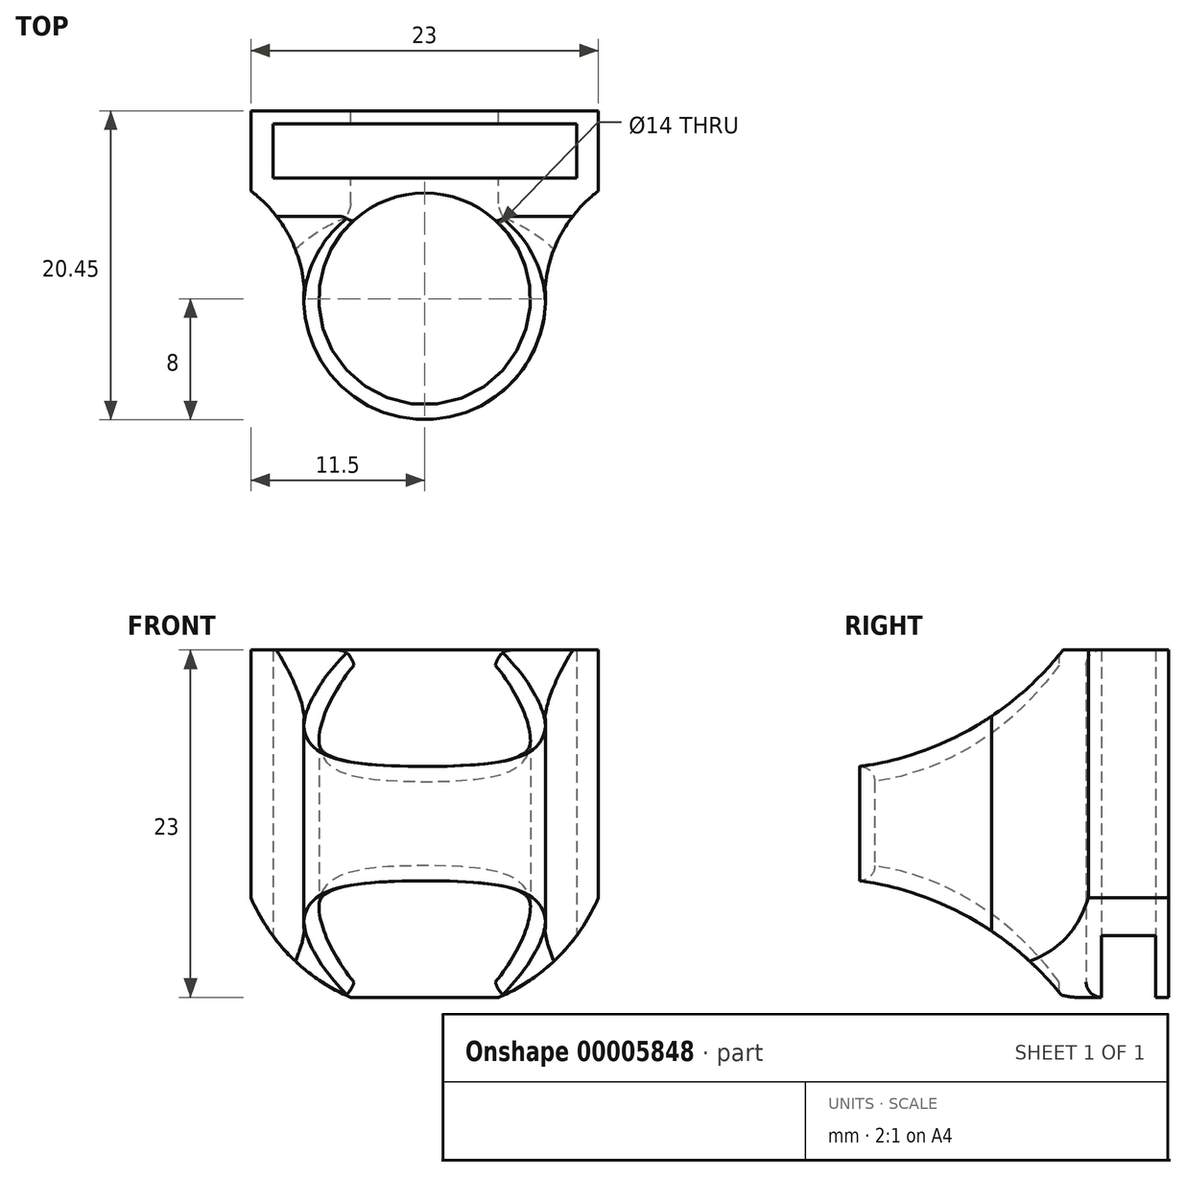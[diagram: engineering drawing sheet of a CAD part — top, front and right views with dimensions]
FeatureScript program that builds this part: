
annotation { "Feature Type Name" : "Feature", "Feature Type Description" : "" }
export const myFeature = defineFeature(function(context is Context, id is Id, definition is map)
    precondition{}
    {
        {
            var Q0;
            Q0=qCreatedBy(makeId("Top.planeOp"),FACE);
            var sketch = newSketch(context, id + "F0", { "sketchPlane" : qUnion([Q0])});
            skCircle(sketch, "E0", {"center": v(0, 0) * mm, "radius": 7 * mm});
            skArc(sketch, "E1", {"start": v(-7.97, 0.72) * mm, "mid": v(0, -8) * mm, "end": v(7.97, 0.72) * mm});
            skLineSegment(sketch, "E2.rect.bottom", {"start": v(11.5, 7.15) * mm, "end": v(-11.5, 7.15) * mm, "construction": true});
            skLineSegment(sketch, "E2.rect.top", {"start": v(11.5, 12.45) * mm, "end": v(-11.5, 12.45) * mm});
            skLineSegment(sketch, "E2.rect.left", {"start": v(11.5, 7.15) * mm, "end": v(11.5, 12.45) * mm});
            skLineSegment(sketch, "E2.rect.right", {"start": v(-11.5, 7.15) * mm, "end": v(-11.5, 12.45) * mm});
            skPoint(sketch, "E2.rect.middle", {"position": v(0, 9.8) * mm});
            skArc(sketch, "E3", {"start": v(-7.97, 0.72) * mm, "mid": v(-9.05, 4.31) * mm, "end": v(-11.5, 7.15) * mm});
            skLineSegment(sketch, "E4", {"start": v(0, 0) * mm, "end": v(0, 9.8) * mm, "construction": true});
            skLineSegment(sketch, "E5.0.MirrorCS", {"start": v(0, 14.3) * mm, "end": v(0, 4.5) * mm, "construction": true});
            skArc(sketch, "E6.0.MirrorCS", {"start": v(7.97, 0.72) * mm, "mid": v(9.05, 4.31) * mm, "end": v(11.5, 7.15) * mm});
            skLineSegment(sketch, "E7.rect.bottom", {"start": v(10.05, 11.6) * mm, "end": v(-10.05, 11.6) * mm});
            skLineSegment(sketch, "E7.rect.top", {"start": v(10.05, 8) * mm, "end": v(-10.05, 8) * mm});
            skLineSegment(sketch, "E7.rect.left", {"start": v(10.05, 11.6) * mm, "end": v(10.05, 8) * mm});
            skLineSegment(sketch, "E7.rect.right", {"start": v(-10.05, 11.6) * mm, "end": v(-10.05, 8) * mm});
            skSolve(sketch);
        }
        {
            var Q0;
            Q0=makeQuery(id+"F0.imprint","IMPRINT",FACE,{"disambiguationData":[TD([[makeQuery(id+"F0.imprint","IMPRINT",EDGE,{"derivedFrom":sQuery(id+"F0.wireOp",EDGE,"E0")}),-1.0]])]});
            extrude(context, id + "F1", {"entities" : qUnion([Q0]), "depth" : 23 * mm});
        }
        {
            var Q0;
            Q0=makeQuery(id+"F1.opExtrude","SWEPT_FACE",FACE,{"disambiguationData":[OSD([sQuery(id+"F0.wireOp",EDGE,"E2.rect.top")])]});
            var sketch = newSketch(context, id + "F2", { "sketchPlane" : qUnion([Q0])});
            skLineSegment(sketch, "E8", {"start": v(11.5, 11.5) * mm, "end": v(0, 11.5) * mm, "construction": true});
            skCircle(sketch, "E9", {"center": v(0, 11.5) * mm, "radius": 12.5 * mm});
            skSolve(sketch);
        }
        {
            var Q0;
            {var subQ0=sQuery(id+"F0.wireOp",EDGE,"E2.rect.top");var subQ1=makeQuery(id+"F1.opExtrude","CAP_EDGE",EDGE,{"disambiguationData":[OSD([subQ0])],"isStart":false});var subQ2=sQuery(id+"F2.wireOp",EDGE,"E9");var subQ3=makeQuery(id+"F2.imprint","INTERSECT",VERTEX,{"disambiguationData":[OD(0.0)],"derivedFrom":[subQ1,subQ2]});Q0=makeQuery(id+"F2.imprint","IMPRINT",FACE,{"disambiguationData":[TD([[makeQuery(id+"F2.imprint","IMPRINT",EDGE,{"disambiguationData":[TD([[subQ3,1.0]])],"derivedFrom":subQ2}),-1.0]])]});}
            var Q1;
            {var subQ0=sQuery(id+"F0.wireOp",EDGE,"E2.rect.top");var subQ1=makeQuery(id+"F1.opExtrude","CAP_EDGE",EDGE,{"disambiguationData":[OSD([subQ0])],"isStart":false});var subQ2=sQuery(id+"F2.wireOp",EDGE,"E9");var subQ3=makeQuery(id+"F2.imprint","INTERSECT",VERTEX,{"disambiguationData":[OD(1.0)],"derivedFrom":[subQ1,subQ2]});Q1=makeQuery(id+"F2.imprint","IMPRINT",FACE,{"disambiguationData":[TD([[makeQuery(id+"F2.imprint","IMPRINT",EDGE,{"disambiguationData":[TD([[subQ3,-1.0]])],"derivedFrom":subQ2}),-1.0]])]});}
            var Q2;
            {var subQ0=sQuery(id+"F0.wireOp",EDGE,"E2.rect.top");var subQ1=makeQuery(id+"F1.opExtrude","CAP_EDGE",EDGE,{"disambiguationData":[OSD([subQ0])],"isStart":true});var subQ2=sQuery(id+"F2.wireOp",EDGE,"E9");var subQ3=makeQuery(id+"F2.imprint","INTERSECT",VERTEX,{"disambiguationData":[OD(0.0)],"derivedFrom":[subQ1,subQ2]});Q2=makeQuery(id+"F2.imprint","IMPRINT",FACE,{"disambiguationData":[TD([[makeQuery(id+"F2.imprint","IMPRINT",EDGE,{"disambiguationData":[TD([[subQ3,1.0]])],"derivedFrom":subQ2}),-1.0]])]});}
            var Q3;
            {var subQ0=sQuery(id+"F0.wireOp",EDGE,"E2.rect.top");var subQ1=makeQuery(id+"F1.opExtrude","CAP_EDGE",EDGE,{"disambiguationData":[OSD([subQ0])],"isStart":true});var subQ2=sQuery(id+"F2.wireOp",EDGE,"E9");var subQ3=makeQuery(id+"F2.imprint","INTERSECT",VERTEX,{"disambiguationData":[OD(1.0)],"derivedFrom":[subQ1,subQ2]});Q3=makeQuery(id+"F2.imprint","IMPRINT",FACE,{"disambiguationData":[TD([[makeQuery(id+"F2.imprint","IMPRINT",EDGE,{"disambiguationData":[TD([[subQ3,-1.0]])],"derivedFrom":subQ2}),-1.0]])]});}
            extrude(context, id + "F3", {"entities" : qUnion([Q0, Q1, Q2, Q3]), "operationType" : NewBodyOperationType.REMOVE, "oppositeDirection" : true, "depth" : 25 * mm});
        }
        {
            var Q0;
            Q0=makeQuery(id+"F1.opExtrude","SWEPT_FACE",FACE,{"disambiguationData":[OSD([sQuery(id+"F0.wireOp",EDGE,"E2.rect.left")])]});
            var sketch = newSketch(context, id + "F4", { "sketchPlane" : qUnion([Q0])});
            skLineSegment(sketch, "E10", {"start": v(12.45, 11.5) * mm, "end": v(-12.92, 11.5) * mm, "construction": true});
            skArc(sketch, "E11", {"start": v(-10.52, 15.1) * mm, "mid": v(0.12, 18.22) * mm, "end": v(7.64, 26.37) * mm});
            skLineSegment(sketch, "E12", {"start": v(7.64, 26.37) * mm, "end": v(-10.52, 26.37) * mm});
            skLineSegment(sketch, "E13", {"start": v(-10.52, 26.37) * mm, "end": v(-10.52, 15.1) * mm});
            skLineSegment(sketch, "E14.0.MirrorCS", {"start": v(7.64, -3.37) * mm, "end": v(-10.52, -3.37) * mm});
            skLineSegment(sketch, "E15.0.MirrorCS", {"start": v(-10.52, -3.37) * mm, "end": v(-10.52, 7.9) * mm});
            skArc(sketch, "E16.0.MirrorCS", {"start": v(-10.52, 7.9) * mm, "mid": v(0.12, 4.78) * mm, "end": v(7.64, -3.37) * mm});
            skSolve(sketch);
        }
        {
            var Q0;
            Q0=makeQuery(id+"F4.imprint","IMPRINT",FACE,{"disambiguationData":[TD([[makeQuery(id+"F4.imprint","IMPRINT",EDGE,{"derivedFrom":sQuery(id+"F4.wireOp",EDGE,"E11")}),1.0]])]});
            var Q1;
            Q1=makeQuery(id+"F4.imprint","IMPRINT",FACE,{"disambiguationData":[TD([[makeQuery(id+"F4.imprint","IMPRINT",EDGE,{"derivedFrom":sQuery(id+"F4.wireOp",EDGE,"E14.0.MirrorCS")}),-1.0]])]});
            extrude(context, id + "F5", {"entities" : qUnion([Q0, Q1]), "operationType" : NewBodyOperationType.REMOVE, "oppositeDirection" : true, "depth" : 25 * mm});
        }
        {
            var Q0;
            Q0=makeQuery(id+"F5.boolean.opBoolean","INTERSECT",EDGE,{"derivedFrom":[makeQuery(id+"F1.opExtrude","SWEPT_FACE",FACE,{"disambiguationData":[OSD([sQuery(id+"F0.wireOp",EDGE,"E0")])]}),makeQuery(id+"F5.opExtrude","SWEPT_FACE",FACE,{"disambiguationData":[OSD([sQuery(id+"F4.wireOp",EDGE,"E11")])]})]});
            var Q1;
            Q1=makeQuery(id+"F3.boolean.opBoolean","SPLIT",EDGE,{"disambiguationData":[OD(1.0)],"derivedFrom":makeQuery(id+"F1.opExtrude","CAP_EDGE",EDGE,{"disambiguationData":[OSD([sQuery(id+"F0.wireOp",EDGE,"E0")])],"isStart":false})});
            var Q2;
            Q2=makeQuery(id+"F3.boolean.opBoolean","SPLIT",EDGE,{"disambiguationData":[OD(1.0)],"derivedFrom":makeQuery(id+"F1.opExtrude","CAP_EDGE",EDGE,{"disambiguationData":[OSD([sQuery(id+"F0.wireOp",EDGE,"E0")])],"isStart":true})});
            var Q3;
            Q3=makeQuery(id+"F5.boolean.opBoolean","INTERSECT",EDGE,{"derivedFrom":[makeQuery(id+"F1.opExtrude","SWEPT_FACE",FACE,{"disambiguationData":[OSD([sQuery(id+"F0.wireOp",EDGE,"E0")])]}),makeQuery(id+"F5.opExtrude","SWEPT_FACE",FACE,{"disambiguationData":[OSD([sQuery(id+"F4.wireOp",EDGE,"E16.0.MirrorCS")])]})]});
            fillet(context, id + "F6", {"entities" : qUnion([Q0, Q1, Q2, Q3]), "radius" : 1 * mm, "tangentPropagation" : true, "allowEdgeOverflow" : false});
        }
    });
